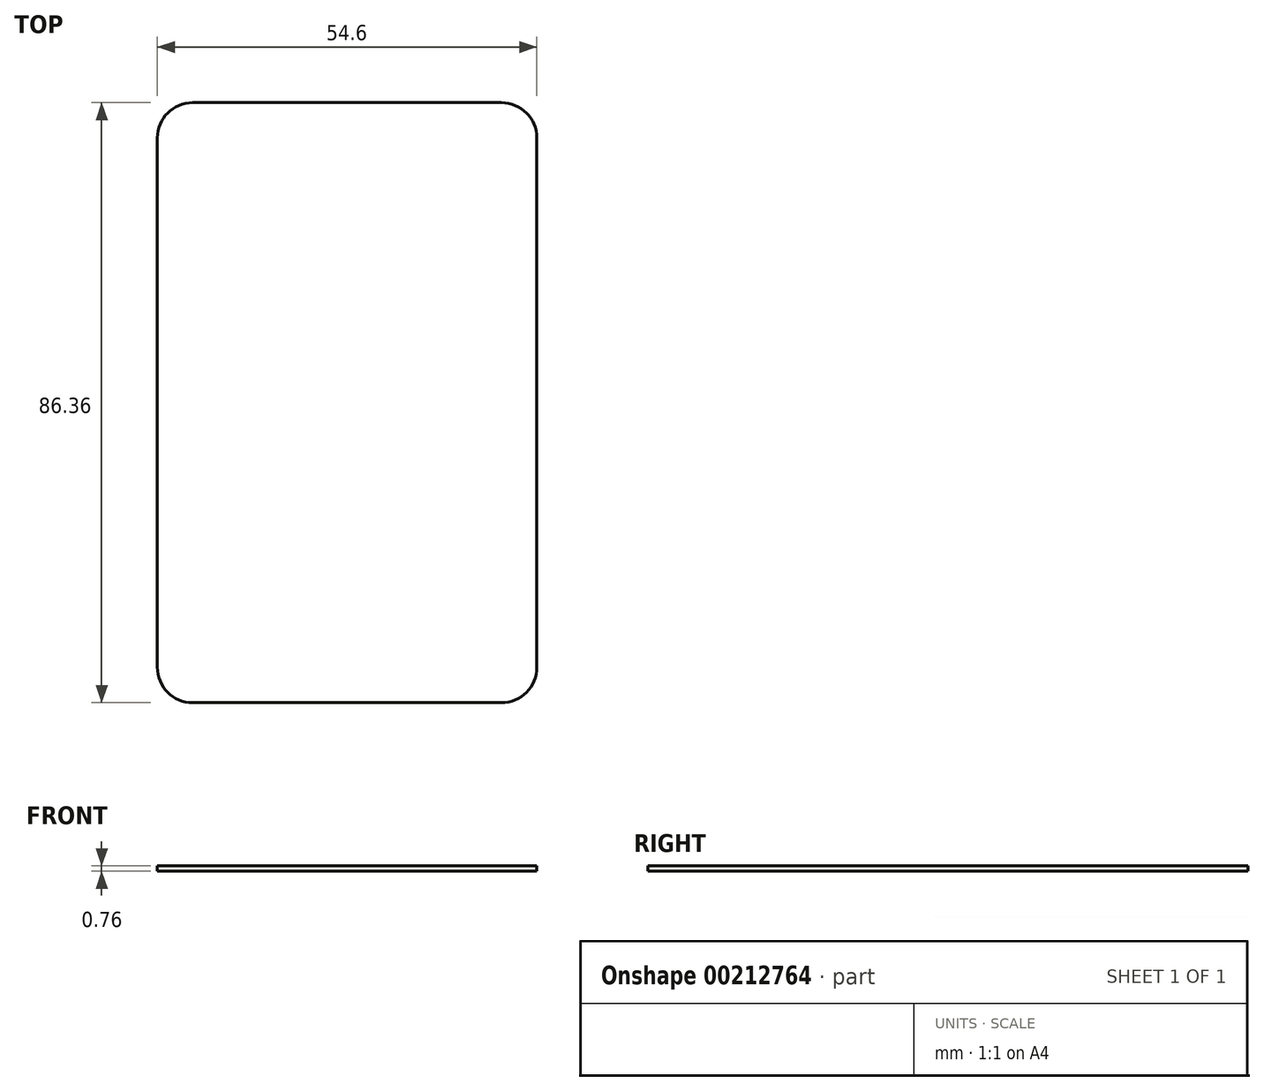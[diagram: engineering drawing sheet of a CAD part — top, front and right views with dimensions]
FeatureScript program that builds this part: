
annotation { "Feature Type Name" : "Feature", "Feature Type Description" : "" }
export const myFeature = defineFeature(function(context is Context, id is Id, definition is map)
    precondition{}
    {
        {
            var Q0;
            Q0=qCreatedBy(makeId("Top.planeOp"),FACE);
            var sketch = newSketch(context, id + "F0", { "sketchPlane" : qUnion([Q0])});
            skLineSegment(sketch, "E0.bottom", {"start": v(-27.3, 43.18) * mm, "end": v(27.3, 43.18) * mm});
            skLineSegment(sketch, "E0.top", {"start": v(-27.3, -43.18) * mm, "end": v(27.3, -43.18) * mm});
            skLineSegment(sketch, "E0.left", {"start": v(-27.3, 43.18) * mm, "end": v(-27.3, -43.18) * mm});
            skLineSegment(sketch, "E0.right", {"start": v(27.3, 43.18) * mm, "end": v(27.3, -43.18) * mm});
            skPoint(sketch, "E0.middle", {"position": v(0, 0) * mm});
            skSolve(sketch);
        }
        {
            var Q0;
            Q0=makeQuery(id+"F0.imprint","IMPRINT",FACE,{"disambiguationData":[TD([[makeQuery(id+"F0.imprint","IMPRINT",EDGE,{"derivedFrom":sQuery(id+"F0.wireOp",EDGE,"E0.bottom")}),-1.0]])]});
            extrude(context, id + "F1", {"entities" : qUnion([Q0]), "depth" : 0.76 * mm, "offsetDistance" : 25.4 * mm});
        }
        {
            var Q0;
            Q0=makeQuery(id+"F1.opExtrude","SWEPT_EDGE",EDGE,{"disambiguationData":[OSD([sQuery(id+"F0.wireOp",EDGE,"E0.top"),sQuery(id+"F0.wireOp",EDGE,"E0.right")])]});
            var Q1;
            Q1=makeQuery(id+"F1.opExtrude","SWEPT_EDGE",EDGE,{"disambiguationData":[OSD([sQuery(id+"F0.wireOp",EDGE,"E0.top"),sQuery(id+"F0.wireOp",EDGE,"E0.left")])]});
            var Q2;
            Q2=makeQuery(id+"F1.opExtrude","SWEPT_EDGE",EDGE,{"disambiguationData":[OSD([sQuery(id+"F0.wireOp",EDGE,"E0.bottom"),sQuery(id+"F0.wireOp",EDGE,"E0.right")])]});
            var Q3;
            Q3=makeQuery(id+"F1.opExtrude","SWEPT_EDGE",EDGE,{"disambiguationData":[OSD([sQuery(id+"F0.wireOp",EDGE,"E0.bottom"),sQuery(id+"F0.wireOp",EDGE,"E0.left")])]});
            fillet(context, id + "F2", {"entities" : qUnion([Q0, Q1, Q2, Q3]), "radius" : 5.08 * mm, "tangentPropagation" : true, "allowEdgeOverflow" : false});
        }
    });
